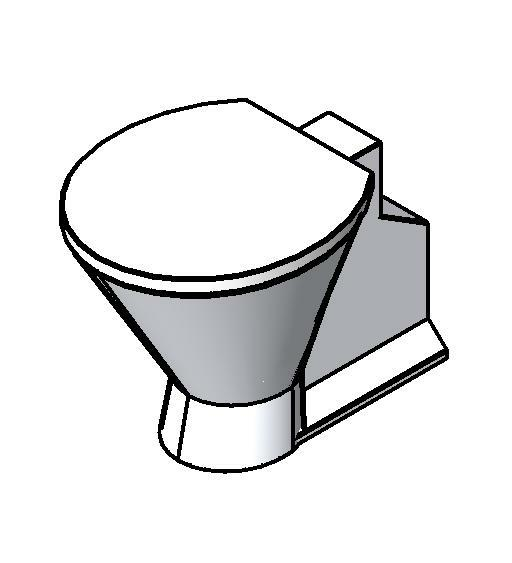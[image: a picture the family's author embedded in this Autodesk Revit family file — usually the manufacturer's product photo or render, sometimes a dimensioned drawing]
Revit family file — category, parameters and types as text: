
# Revit family: Deca_Cuba sobrepor retangular 50cm_Cuba Slim_L.23050
name_source: partatom
category: Plumbing Fixtures
units: mm (PartAtom-declared; Revit-internal decimal feet)

## family parameters
Cut with Voids When Loaded = No
Host = Face
Part Type = Normal
Room Calculation Point = No
Round Connector Dimension = Use Radius
Shared = No

## types (4) — shared parameters
Acompanha o Produto = Acabamento da válvula cerâmica/Smartblock
Aprovado por = quattroD
Atendimento ao Cliente = 0800-0117073
Categoria = CUBAS
Composição Básica = Composição Básica: Argila / Feldispato / Caulim / Vidrados e corantes inorgânicos / Plásticos de Engenharia.
Composição Componente = PEBD
Cores Componente = transparente
Criado por = quattroD
Código Pai = L.23050.17
Linha = CUBA SLIM
Manufacturer = DECA
Norma = NBR 16728-1 / NBR 16728-2
Peso Líquido (Kg) = 7.8
Pressão máx. funcionamento = 40mca
Pressão mín. funcionamento = 3mca
Saída de Esgoto = válvula curta
Segmento = LUXO
URL = www.deca.com.br
zero-valued in all types: CWFU, Default Elevation, Diâmetro Ponto de Esgoto, Diâmetro Água Fria, Raio Ponto de Esgoto, Raio Água Fria, WFU

## per-type parameters (varying)
| type | Cor Interna | Cor Principal | Informações Complementares | Material | Model |
| L.23050.17_Branco | Branco | Branco | Esmalte Protekto | Deca_Branco | L.23050.17 |
| L.23050.26_Barbante | Barbante | Barbante |  | Deca_Barbante | L.23050.26 |
| L.23050.85_Cinza Antracite | Cinza Soft Antracite | Antracite |  | Deca_Cinza Antracite | L.23050.85 |
| L.23050.94_Ébano Fosco | Ébano Fosco | Ébano Fosco |  | Deca_Ébano Fosco | L.23050.94 |

## geometry (parser evidence)
native form markers: Sweep x3
no freeform markers — native parametric forms only
